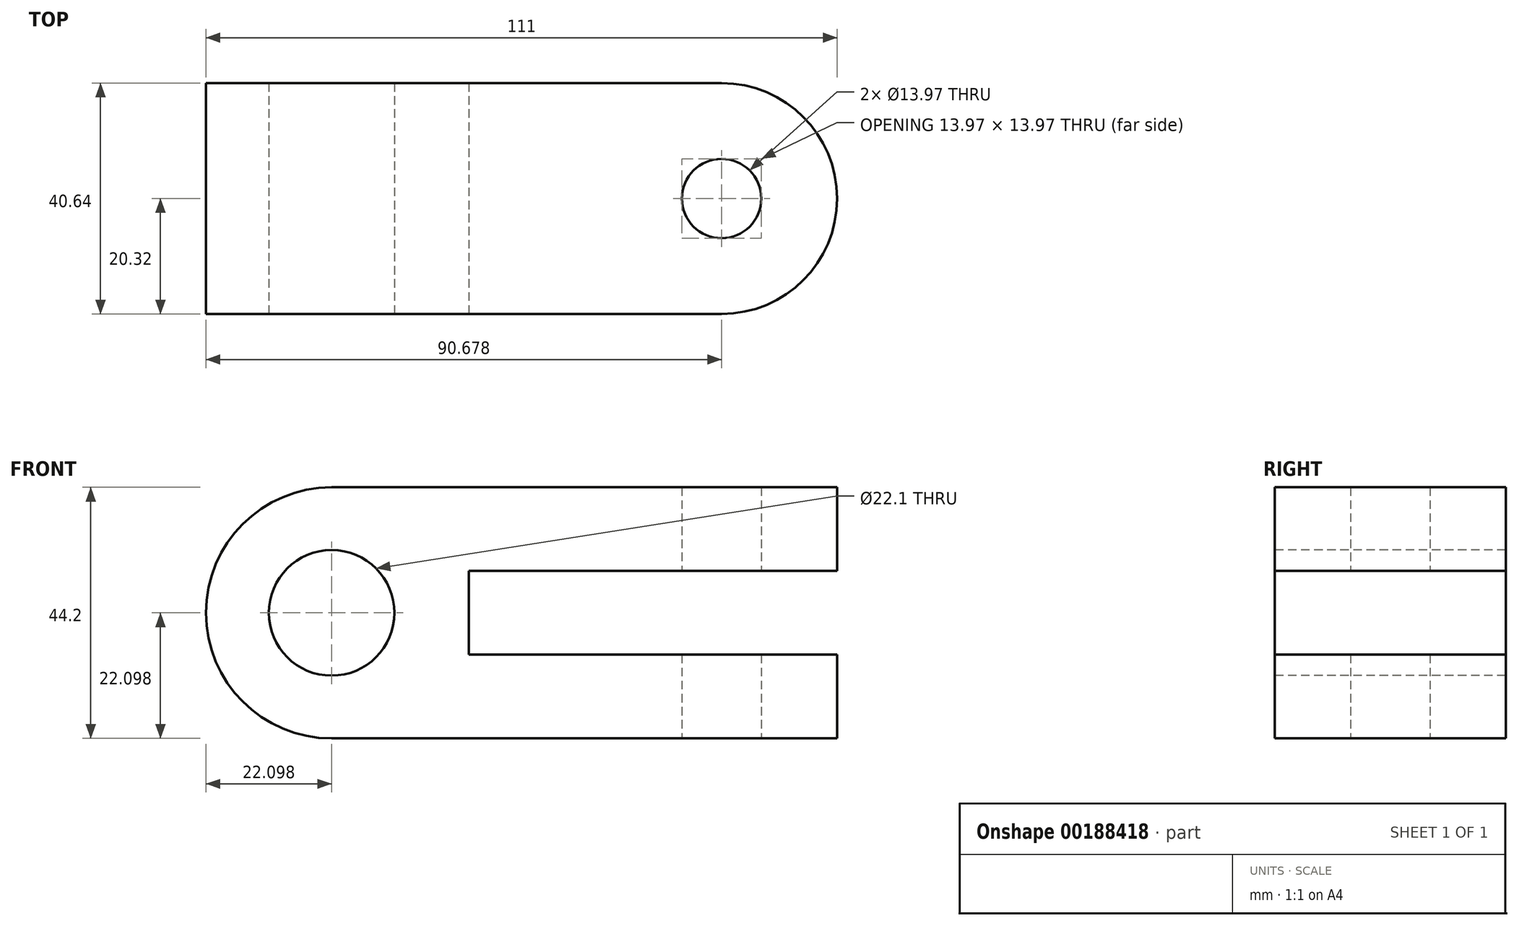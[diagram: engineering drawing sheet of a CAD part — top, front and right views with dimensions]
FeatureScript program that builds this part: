
annotation { "Feature Type Name" : "Feature", "Feature Type Description" : "" }
export const myFeature = defineFeature(function(context is Context, id is Id, definition is map)
    precondition{}
    {
        {
            var Q0;
            Q0=qCreatedBy(makeId("Top.planeOp"),FACE);
            var sketch = newSketch(context, id + "F0", { "sketchPlane" : qUnion([Q0])});
            skLineSegment(sketch, "E0.bottom", {"start": v(0, 0) * mm, "end": v(111, 0) * mm});
            skLineSegment(sketch, "E0.top", {"start": v(0, 40.64) * mm, "end": v(111, 40.64) * mm});
            skLineSegment(sketch, "E0.left", {"start": v(0, 0) * mm, "end": v(0, 40.64) * mm});
            skLineSegment(sketch, "E0.right", {"start": v(111, 0) * mm, "end": v(111, 40.64) * mm});
            skCircle(sketch, "E1", {"center": v(90.68, 20.32) * mm, "radius": 20.32 * mm});
            skCircle(sketch, "E2", {"center": v(90.68, 20.32) * mm, "radius": 6.99 * mm});
            skSolve(sketch);
        }
        {
            var Q0;
            Q0=qCreatedBy(makeId("Front.planeOp"),FACE);
            var sketch = newSketch(context, id + "F1", { "sketchPlane" : qUnion([Q0])});
            skLineSegment(sketch, "E3.bottom", {"start": v(0, 0) * mm, "end": v(111, 0) * mm});
            skLineSegment(sketch, "E3.top", {"start": v(0, 44.2) * mm, "end": v(111, 44.2) * mm});
            skLineSegment(sketch, "E3.left", {"start": v(0, 0) * mm, "end": v(0, 44.2) * mm});
            skLineSegment(sketch, "E3.right", {"start": v(111, 0) * mm, "end": v(111, 44.2) * mm});
            skPoint(sketch, "E4.endSnap0", {"position": v(0, 22.1) * mm});
            skCircle(sketch, "E5", {"center": v(22.1, 22.1) * mm, "radius": 22.1 * mm});
            skCircle(sketch, "E6", {"center": v(22.1, 22.1) * mm, "radius": 11.05 * mm});
            skLineSegment(sketch, "E7.bottom", {"start": v(46.23, 29.46) * mm, "end": v(111, 29.46) * mm});
            skLineSegment(sketch, "E7.top", {"start": v(46.23, 14.73) * mm, "end": v(111, 14.73) * mm});
            skLineSegment(sketch, "E7.left", {"start": v(46.23, 29.46) * mm, "end": v(46.23, 14.73) * mm});
            skLineSegment(sketch, "E7.right", {"start": v(111, 29.46) * mm, "end": v(111, 14.73) * mm});
            skLineSegment(sketch, "E8", {"start": v(111, 44.2) * mm, "end": v(111, 29.46) * mm});
            skSolve(sketch);
        }
        {
            var Q0;
            {var subQ0=sQuery(id+"F0.wireOp",EDGE,"E0.left");Q0=makeQuery(id+"F0.imprint","IMPRINT",FACE,{"disambiguationData":[TD([[makeQuery(id+"F0.imprint","IMPRINT",EDGE,{"derivedFrom":subQ0}),-1.0]])]});}
            var Q1;
            Q1=makeQuery(id+"F0.imprint","IMPRINT",FACE,{"disambiguationData":[TD([[makeQuery(id+"F0.imprint","IMPRINT",EDGE,{"derivedFrom":sQuery(id+"F0.wireOp",EDGE,"E2")}),-1.0]])]});
            extrude(context, id + "F2", {"entities" : qUnion([Q0, Q1]), "depth" : 44.2 * mm});
        }
        {
            var Q0;
            Q0=makeQuery(id+"F1.imprint","IMPRINT",FACE,{"disambiguationData":[TD([[makeQuery(id+"F1.imprint","IMPRINT",EDGE,{"derivedFrom":sQuery(id+"F1.wireOp",EDGE,"E6")}),1.0]])]});
            extrude(context, id + "F3", {"entities" : qUnion([Q0]), "operationType" : NewBodyOperationType.REMOVE, "endBound" : BoundingType.THROUGH_ALL, "oppositeDirection" : true, "depth" : 40.64 * mm});
        }
        {
            var Q0;
            Q0=makeQuery(id+"F2.opExtrude","CAP_EDGE",EDGE,{"disambiguationData":[OSD([sQuery(id+"F0.wireOp",EDGE,"E0.left")])],"isStart":false});
            fillet(context, id + "F4", {"entities" : qUnion([Q0]), "radius" : 22.1 * mm, "tangentPropagation" : true, "allowEdgeOverflow" : false});
        }
        {
            var Q0;
            Q0=makeQuery(id+"F2.opExtrude","CAP_EDGE",EDGE,{"disambiguationData":[OSD([sQuery(id+"F0.wireOp",EDGE,"E0.left")])],"isStart":true});
            fillet(context, id + "F5", {"entities" : qUnion([Q0]), "radius" : 22.1 * mm, "tangentPropagation" : true, "allowEdgeOverflow" : false});
        }
        {
            var Q0;
            Q0=makeQuery(id+"F1.imprint","IMPRINT",FACE,{"disambiguationData":[TD([[makeQuery(id+"F1.imprint","IMPRINT",EDGE,{"derivedFrom":sQuery(id+"F1.wireOp",EDGE,"E7.bottom")}),-1.0]])]});
            extrude(context, id + "F6", {"entities" : qUnion([Q0]), "operationType" : NewBodyOperationType.REMOVE, "endBound" : BoundingType.THROUGH_ALL, "oppositeDirection" : true, "depth" : 25.4 * mm});
        }
    });
